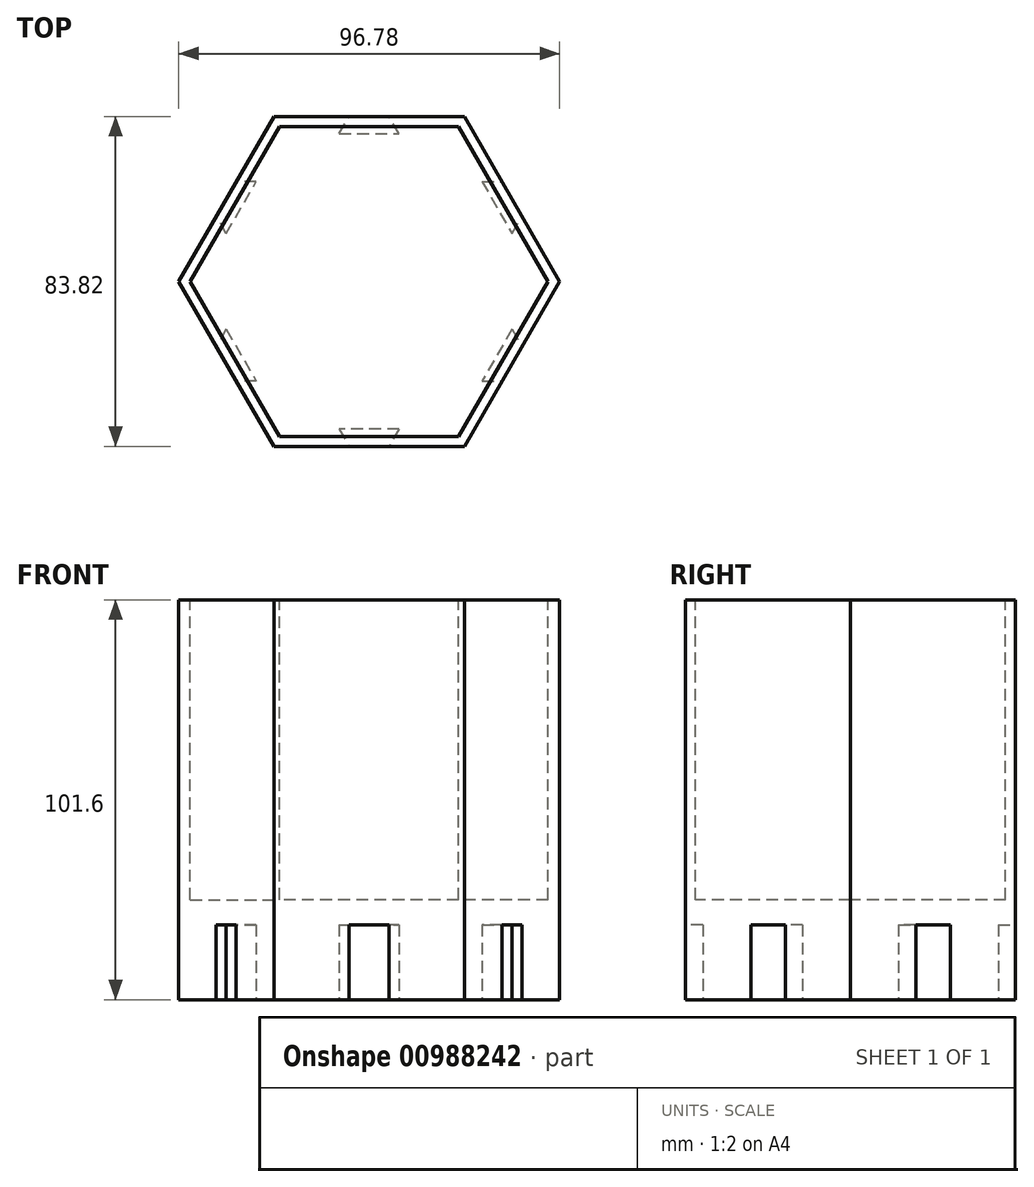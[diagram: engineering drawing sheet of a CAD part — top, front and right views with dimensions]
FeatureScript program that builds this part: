
annotation { "Feature Type Name" : "Feature", "Feature Type Description" : "" }
export const myFeature = defineFeature(function(context is Context, id is Id, definition is map)
    precondition{}
    {
        {
            var Q0;
            Q0=qCreatedBy(makeId("Top.planeOp"),FACE);
            var sketch = newSketch(context, id + "F0", { "sketchPlane" : qUnion([Q0])});
            skCircle(sketch, "E0.cCircle", {"center": v(0, 0) * mm, "radius": 41.9 * mm, "construction": true});
            skLineSegment(sketch, "E0.0", {"start": v(24.2, -41.91) * mm, "end": v(-24.2, -41.91) * mm});
            skLineSegment(sketch, "E0.1", {"start": v(-24.2, -41.91) * mm, "end": v(-48.4, 0) * mm});
            skLineSegment(sketch, "E0.2", {"start": v(-48.4, 0) * mm, "end": v(-24.2, 41.91) * mm});
            skLineSegment(sketch, "E0.3", {"start": v(-24.2, 41.9) * mm, "end": v(24.2, 41.91) * mm});
            skLineSegment(sketch, "E0.4", {"start": v(24.2, 41.91) * mm, "end": v(48.4, 0) * mm});
            skLineSegment(sketch, "E0.5", {"start": v(48.4, 0) * mm, "end": v(24.2, -41.91) * mm});
            skPoint(sketch, "E0.0.midPoint", {"position": v(0, -41.91) * mm});
            skSolve(sketch);
        }
        {
            var Q0;
            Q0=makeQuery(id+"F0.imprint","IMPRINT",FACE,{"disambiguationData":[TD([[makeQuery(id+"F0.imprint","IMPRINT",EDGE,{"derivedFrom":sQuery(id+"F0.wireOp",EDGE,"E0.0")}),-1.0]])]});
            extrude(context, id + "F1", {"entities" : qUnion([Q0]), "depth" : 101.6 * mm, "offsetDistance" : 25.4 * mm});
        }
        {
            var Q0;
            Q0=makeQuery(id+"F1.opExtrude","CAP_FACE",FACE,{"disambiguationData":[OSD([sQuery(id+"F0.wireOp",EDGE,"E0.0"),sQuery(id+"F0.wireOp",EDGE,"E0.1"),sQuery(id+"F0.wireOp",EDGE,"E0.2"),sQuery(id+"F0.wireOp",EDGE,"E0.3"),sQuery(id+"F0.wireOp",EDGE,"E0.4"),sQuery(id+"F0.wireOp",EDGE,"E0.5")])],"isStart":false});
            var sketch = newSketch(context, id + "F2", { "sketchPlane" : qUnion([Q0])});
            skCircle(sketch, "E1.cCircle", {"center": v(0, 0) * mm, "radius": 39.37 * mm, "construction": true});
            skLineSegment(sketch, "E1.0", {"start": v(22.73, -39.37) * mm, "end": v(-22.73, -39.37) * mm});
            skLineSegment(sketch, "E1.1", {"start": v(-22.73, -39.37) * mm, "end": v(-45.46, 0) * mm});
            skLineSegment(sketch, "E1.2", {"start": v(-45.46, 0) * mm, "end": v(-22.73, 39.37) * mm});
            skLineSegment(sketch, "E1.3", {"start": v(-22.73, 39.37) * mm, "end": v(22.73, 39.37) * mm});
            skLineSegment(sketch, "E1.4", {"start": v(22.73, 39.37) * mm, "end": v(45.46, 0) * mm});
            skLineSegment(sketch, "E1.5", {"start": v(45.46, 0) * mm, "end": v(22.73, -39.37) * mm});
            skPoint(sketch, "E1.0.midPoint", {"position": v(0, -39.37) * mm});
            skSolve(sketch);
        }
        {
            var Q0;
            Q0=makeQuery(id+"F2.imprint","IMPRINT",FACE,{"disambiguationData":[TD([[makeQuery(id+"F2.imprint","IMPRINT",EDGE,{"derivedFrom":sQuery(id+"F2.wireOp",EDGE,"E1.0")}),-1.0]])]});
            extrude(context, id + "F3", {"entities" : qUnion([Q0]), "operationType" : NewBodyOperationType.REMOVE, "oppositeDirection" : true, "depth" : 76.2 * mm, "offsetDistance" : 25.4 * mm});
        }
        {
            var Q0;
            Q0=makeQuery(id+"F1.opExtrude","CAP_FACE",FACE,{"disambiguationData":[OSD([sQuery(id+"F0.wireOp",EDGE,"E0.0"),sQuery(id+"F0.wireOp",EDGE,"E0.1"),sQuery(id+"F0.wireOp",EDGE,"E0.2"),sQuery(id+"F0.wireOp",EDGE,"E0.3"),sQuery(id+"F0.wireOp",EDGE,"E0.4"),sQuery(id+"F0.wireOp",EDGE,"E0.5")])],"isStart":true});
            var sketch = newSketch(context, id + "F4", { "sketchPlane" : qUnion([Q0])});
            skLineSegment(sketch, "E2.0", {"start": v(48.4, 0) * mm, "end": v(24.2, 41.91) * mm});
            skLineSegment(sketch, "E3", {"start": v(36.3, 20.95) * mm, "end": v(-36.3, -20.95) * mm});
            skLineSegment(sketch, "E4", {"start": v(32.49, 18.76) * mm, "end": v(28.68, 25.35) * mm});
            skLineSegment(sketch, "E5", {"start": v(28.68, 25.35) * mm, "end": v(33.76, 25.35) * mm});
            skLineSegment(sketch, "E6.MirrorCS", {"start": v(36.3, 12.16) * mm, "end": v(38.84, 16.56) * mm});
            skLineSegment(sketch, "E7.MirrorCS", {"start": v(32.49, 18.76) * mm, "end": v(36.3, 12.16) * mm});
            skLineSegment(sketch, "E8", {"start": v(-24.2, 41.91) * mm, "end": v(24.2, -41.91) * mm});
            skLineSegment(sketch, "E9.MirrorCS", {"start": v(-32.49, -18.76) * mm, "end": v(-36.3, -12.16) * mm});
            skLineSegment(sketch, "E10.MirrorCS", {"start": v(-36.3, -12.16) * mm, "end": v(-38.84, -16.56) * mm});
            skLineSegment(sketch, "E11.MirrorCS", {"start": v(-32.49, -18.76) * mm, "end": v(-28.68, -25.35) * mm});
            skLineSegment(sketch, "E12.MirrorCS", {"start": v(-28.68, -25.35) * mm, "end": v(-33.76, -25.35) * mm});
            skLineSegment(sketch, "E13", {"start": v(-36.3, 20.96) * mm, "end": v(36.3, -20.96) * mm});
            skLineSegment(sketch, "E14", {"start": v(0, 41.91) * mm, "end": v(0, -41.91) * mm});
            skLineSegment(sketch, "E15", {"start": v(0, 37.51) * mm, "end": v(-7.62, 37.51) * mm});
            skLineSegment(sketch, "E16", {"start": v(-7.62, 37.51) * mm, "end": v(-5.08, 41.91) * mm});
            skLineSegment(sketch, "E17.MirrorCS", {"start": v(0, 37.51) * mm, "end": v(7.62, 37.51) * mm});
            skLineSegment(sketch, "E18.MirrorCS", {"start": v(7.62, 37.51) * mm, "end": v(5.08, 41.9) * mm});
            skLineSegment(sketch, "E19.MirrorCS", {"start": v(0, -37.51) * mm, "end": v(-7.62, -37.51) * mm});
            skLineSegment(sketch, "E20.MirrorCS", {"start": v(-7.62, -37.51) * mm, "end": v(-5.08, -41.91) * mm});
            skLineSegment(sketch, "E21.MirrorCS", {"start": v(0, -37.51) * mm, "end": v(7.62, -37.51) * mm});
            skLineSegment(sketch, "E22.MirrorCS", {"start": v(7.62, -37.51) * mm, "end": v(5.08, -41.9) * mm});
            skLineSegment(sketch, "E23", {"start": v(-32.49, 18.76) * mm, "end": v(-28.68, 25.35) * mm});
            skLineSegment(sketch, "E24", {"start": v(-28.68, 25.35) * mm, "end": v(-33.76, 25.35) * mm});
            skLineSegment(sketch, "E25", {"start": v(24.2, 41.91) * mm, "end": v(-24.2, -41.91) * mm});
            skLineSegment(sketch, "E26.MirrorCS", {"start": v(32.49, -18.76) * mm, "end": v(36.3, -12.16) * mm});
            skLineSegment(sketch, "E27.MirrorCS", {"start": v(36.3, -12.16) * mm, "end": v(38.84, -16.56) * mm});
            skLineSegment(sketch, "E28.MirrorCS", {"start": v(-32.49, 18.76) * mm, "end": v(-36.3, 12.16) * mm});
            skLineSegment(sketch, "E29.MirrorCS", {"start": v(-36.3, 12.16) * mm, "end": v(-38.84, 16.56) * mm});
            skLineSegment(sketch, "E30.MirrorCS", {"start": v(32.49, -18.76) * mm, "end": v(28.68, -25.35) * mm});
            skLineSegment(sketch, "E31.MirrorCS", {"start": v(28.68, -25.35) * mm, "end": v(33.76, -25.35) * mm});
            skSolve(sketch);
        }
        {
            var Q0;
            {var subQ3=sQuery(id+"F4.wireOp",EDGE,"E15");Q0=makeQuery(id+"F4.imprint","IMPRINT",FACE,{"disambiguationData":[TD([[makeQuery(id+"F4.imprint","IMPRINT",EDGE,{"derivedFrom":subQ3}),-1.0]])]});}
            var Q1;
            {var subQ3=sQuery(id+"F4.wireOp",EDGE,"E17.MirrorCS");Q1=makeQuery(id+"F4.imprint","IMPRINT",FACE,{"disambiguationData":[TD([[makeQuery(id+"F4.imprint","IMPRINT",EDGE,{"derivedFrom":subQ3}),1.0]])]});}
            var Q2;
            {var subQ4=sQuery(id+"F4.wireOp",EDGE,"E4");Q2=makeQuery(id+"F4.imprint","IMPRINT",FACE,{"disambiguationData":[TD([[makeQuery(id+"F4.imprint","IMPRINT",EDGE,{"derivedFrom":subQ4}),-1.0]])]});}
            var Q3;
            {var subQ3=sQuery(id+"F4.wireOp",EDGE,"E6.MirrorCS");Q3=makeQuery(id+"F4.imprint","IMPRINT",FACE,{"disambiguationData":[TD([[makeQuery(id+"F4.imprint","IMPRINT",EDGE,{"derivedFrom":subQ3}),1.0]])]});}
            var Q4;
            {var subQ3=sQuery(id+"F4.wireOp",EDGE,"E26.MirrorCS");Q4=makeQuery(id+"F4.imprint","IMPRINT",FACE,{"disambiguationData":[TD([[makeQuery(id+"F4.imprint","IMPRINT",EDGE,{"derivedFrom":subQ3}),-1.0]])]});}
            var Q5;
            {var subQ3=sQuery(id+"F4.wireOp",EDGE,"E30.MirrorCS");Q5=makeQuery(id+"F4.imprint","IMPRINT",FACE,{"disambiguationData":[TD([[makeQuery(id+"F4.imprint","IMPRINT",EDGE,{"derivedFrom":subQ3}),1.0]])]});}
            var Q6;
            {var subQ3=sQuery(id+"F4.wireOp",EDGE,"E21.MirrorCS");Q6=makeQuery(id+"F4.imprint","IMPRINT",FACE,{"disambiguationData":[TD([[makeQuery(id+"F4.imprint","IMPRINT",EDGE,{"derivedFrom":subQ3}),-1.0]])]});}
            var Q7;
            {var subQ3=sQuery(id+"F4.wireOp",EDGE,"E19.MirrorCS");Q7=makeQuery(id+"F4.imprint","IMPRINT",FACE,{"disambiguationData":[TD([[makeQuery(id+"F4.imprint","IMPRINT",EDGE,{"derivedFrom":subQ3}),1.0]])]});}
            var Q8;
            {var subQ3=sQuery(id+"F4.wireOp",EDGE,"E11.MirrorCS");Q8=makeQuery(id+"F4.imprint","IMPRINT",FACE,{"disambiguationData":[TD([[makeQuery(id+"F4.imprint","IMPRINT",EDGE,{"derivedFrom":subQ3}),-1.0]])]});}
            var Q9;
            {var subQ3=sQuery(id+"F4.wireOp",EDGE,"E9.MirrorCS");Q9=makeQuery(id+"F4.imprint","IMPRINT",FACE,{"disambiguationData":[TD([[makeQuery(id+"F4.imprint","IMPRINT",EDGE,{"derivedFrom":subQ3}),1.0]])]});}
            var Q10;
            {var subQ3=sQuery(id+"F4.wireOp",EDGE,"E23");Q10=makeQuery(id+"F4.imprint","IMPRINT",FACE,{"disambiguationData":[TD([[makeQuery(id+"F4.imprint","IMPRINT",EDGE,{"derivedFrom":subQ3}),1.0]])]});}
            var Q11;
            {var subQ3=sQuery(id+"F4.wireOp",EDGE,"E28.MirrorCS");Q11=makeQuery(id+"F4.imprint","IMPRINT",FACE,{"disambiguationData":[TD([[makeQuery(id+"F4.imprint","IMPRINT",EDGE,{"derivedFrom":subQ3}),-1.0]])]});}
            extrude(context, id + "F5", {"entities" : qUnion([Q0, Q1, Q2, Q3, Q4, Q5, Q6, Q7, Q8, Q9, Q10, Q11]), "operationType" : NewBodyOperationType.REMOVE, "oppositeDirection" : true, "depth" : 19.05 * mm, "offsetDistance" : 25.4 * mm});
        }
    });
